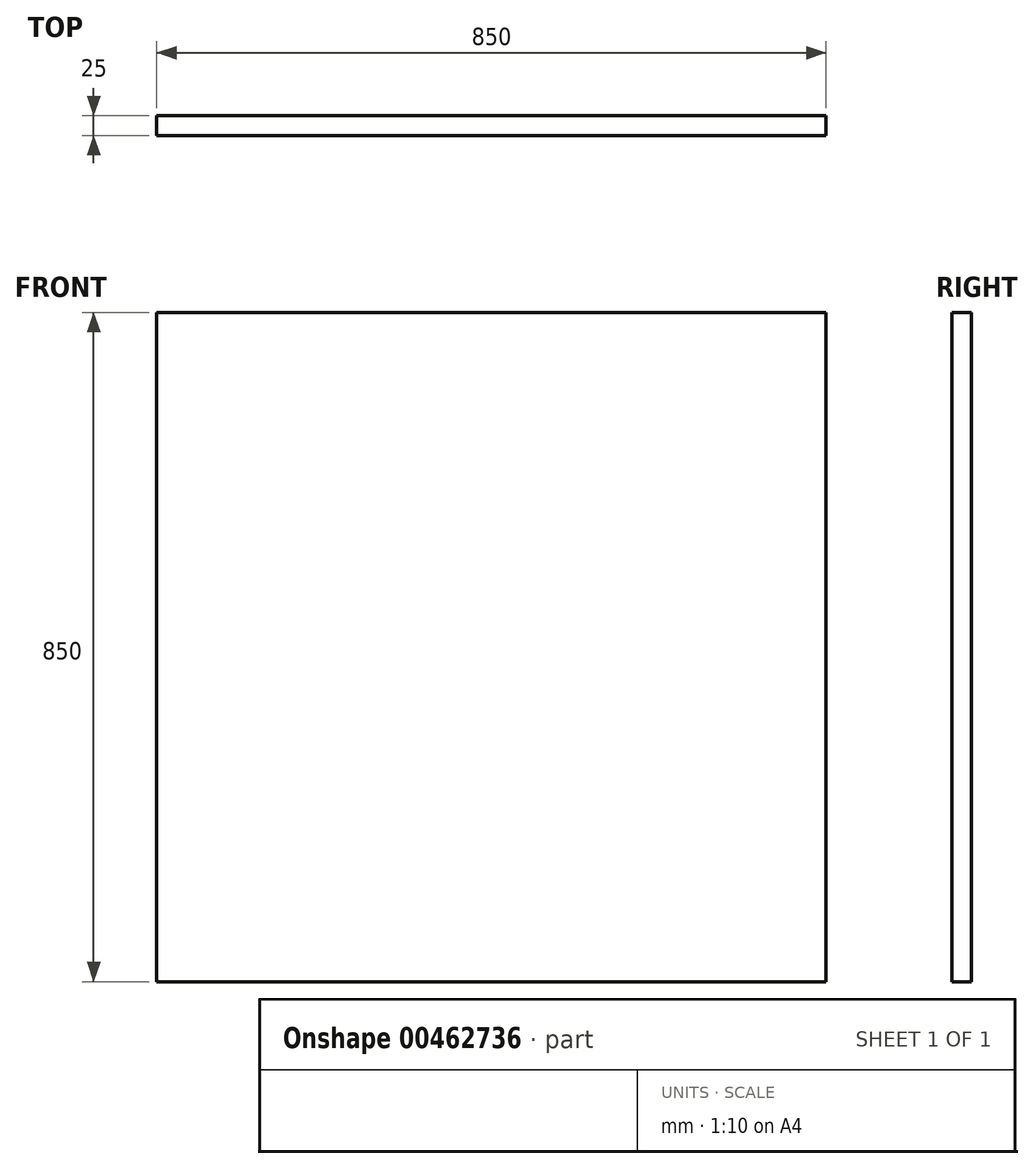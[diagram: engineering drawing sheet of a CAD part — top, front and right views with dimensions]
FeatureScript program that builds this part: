
annotation { "Feature Type Name" : "Feature", "Feature Type Description" : "" }
export const myFeature = defineFeature(function(context is Context, id is Id, definition is map)
    precondition{}
    {
        {
            var Q0;
            Q0=qCreatedBy(makeId("Front.planeOp"),FACE);
            var sketch = newSketch(context, id + "F0", { "sketchPlane" : qUnion([Q0])});
            skLineSegment(sketch, "E0.bottom", {"start": v(425, 425) * mm, "end": v(-425, 425) * mm});
            skLineSegment(sketch, "E0.top", {"start": v(425, -425) * mm, "end": v(-425, -425) * mm});
            skLineSegment(sketch, "E0.left", {"start": v(425, 425) * mm, "end": v(425, -425) * mm});
            skLineSegment(sketch, "E0.right", {"start": v(-425, 425) * mm, "end": v(-425, -425) * mm});
            skPoint(sketch, "E0.middle", {"position": v(0, 0) * mm});
            skSolve(sketch);
        }
        {
            var Q0;
            Q0 = qSketchRegion(id + "F0", true);
            extrude(context, id + "F1", {"entities" : qUnion([Q0]), "depth" : 25 * mm});
        }
    });
